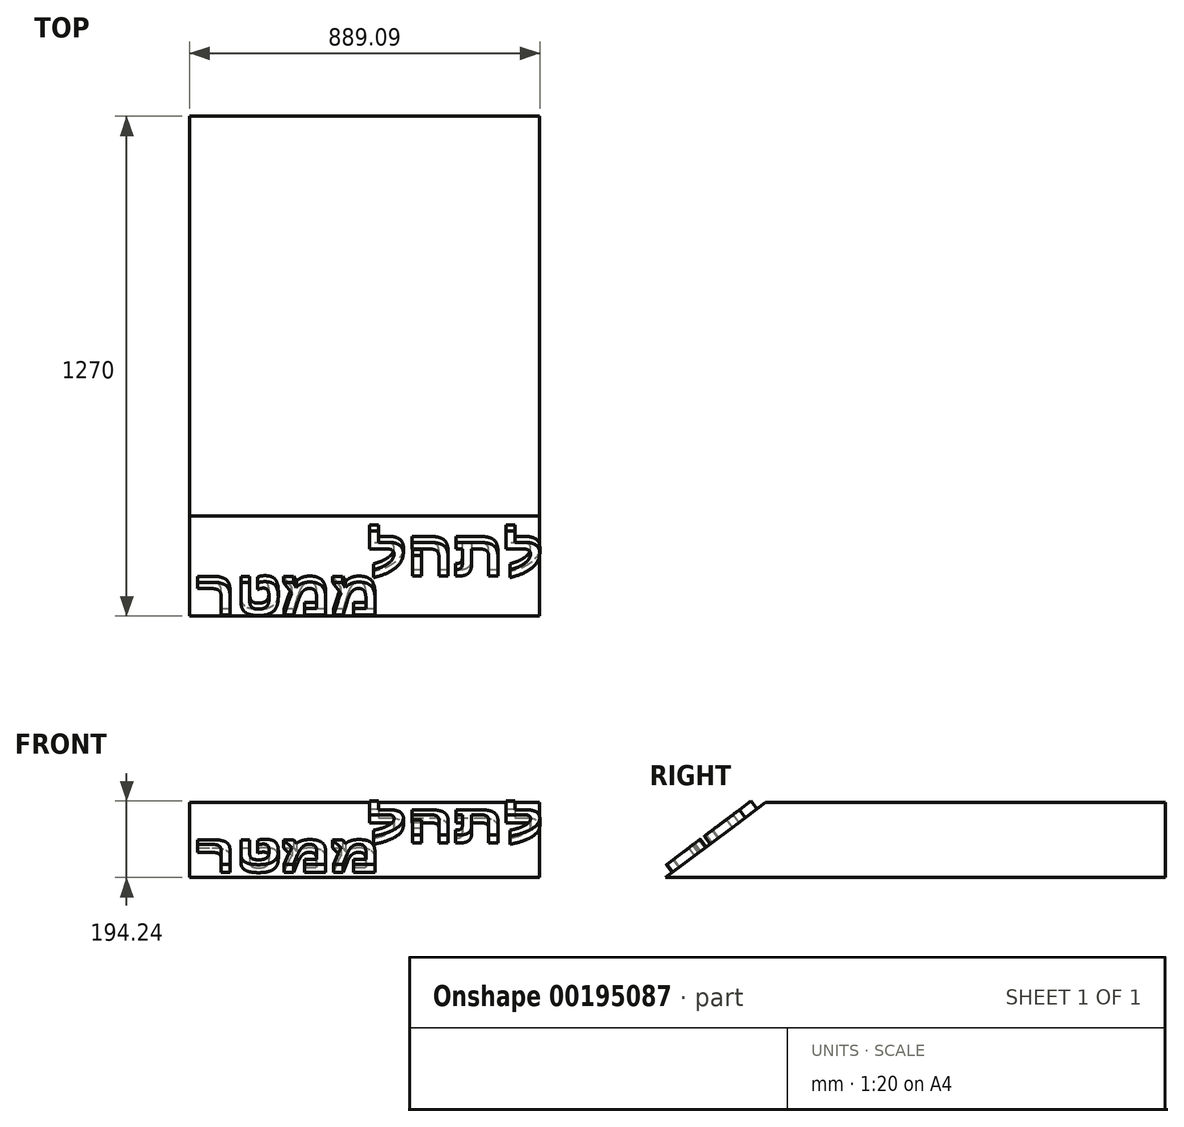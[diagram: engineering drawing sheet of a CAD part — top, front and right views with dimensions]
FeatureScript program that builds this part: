
annotation { "Feature Type Name" : "Feature", "Feature Type Description" : "" }
export const myFeature = defineFeature(function(context is Context, id is Id, definition is map)
    precondition{}
    {
        {
            var Q0;
            Q0=qCreatedBy(makeId("Right.planeOp"),FACE);
            var sketch = newSketch(context, id + "F0", { "sketchPlane" : qUnion([Q0])});
            skLineSegment(sketch, "E0", {"start": v(-38.84, -808.32) * mm, "end": v(-1054.84, -808.32) * mm});
            skLineSegment(sketch, "E1", {"start": v(-1054.84, -808.32) * mm, "end": v(-1308.84, -998.82) * mm});
            skLineSegment(sketch, "E2", {"start": v(-1308.84, -998.82) * mm, "end": v(-38.84, -998.82) * mm});
            skLineSegment(sketch, "E3", {"start": v(-38.84, -998.82) * mm, "end": v(-38.84, -808.32) * mm});
            skSolve(sketch);
        }
        {
            var Q0;
            Q0=makeQuery(id+"F0.imprint","IMPRINT",FACE,{"disambiguationData":[TD([[makeQuery(id+"F0.imprint","IMPRINT",EDGE,{"derivedFrom":sQuery(id+"F0.wireOp",EDGE,"E0")}),1.0]])]});
            extrude(context, id + "F1", {"entities" : qUnion([Q0]), "depth" : 889 * mm, "offsetDistance" : 25.4 * mm, "symmetric" : true});
        }
        {
            var Q0;
            Q0=makeQuery(id+"F1.opExtrude","SWEPT_FACE",FACE,{"disambiguationData":[OSD([sQuery(id+"F0.wireOp",EDGE,"E1")])]});
            var sketch = newSketch(context, id + "F2", { "sketchPlane" : qUnion([Q0])});
            skText(sketch, "E4", { "text": "להתל", "fontName": "Arimo-Bold.ttf"});
            skText(sketch, "E5", { "text": "רטממ", "fontName": "Arimo-Bold.ttf"});
            const initialGuessF2  = {"E4": [0.00552, -1.4999, 1, 0, 0.127], "E5": [-0.42787, -1.6238, 1, 0, 0.1239]};
            skSetInitialGuess(sketch, initialGuessF2);
            skSolve(sketch);
        }
        {
            var Q0;
            Q0=qSketchRegion(id+"F2",true);
            extrude(context, id + "F3", {"entities" : qUnion([Q0]), "operationType" : NewBodyOperationType.ADD, "depth" : 25.4 * mm});
        }
    });
